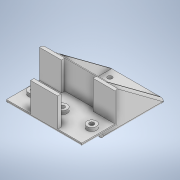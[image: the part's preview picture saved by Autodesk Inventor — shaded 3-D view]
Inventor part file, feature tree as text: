
AUTODESK INVENTOR PART (.ipt)
format: ipt  version: 2020 (Build 240168000, 168)  size: 404,992 bytes
history: native  units: in
note: dims shown in document units (in); Inventor stores cm internally (conversion verified against a paired STEP export)
features: sketch x19, extrude x18, fillet x1
ambient origin geometry x8: Origin, YZ Plane, XZ Plane, XY Plane, X Axis, Y Axis, Z Axis, Center Point
bodies: Solid1 (feature_tree)
feature tree (38):
  extrude  "Extrusion1"  Depth=1.2756in
  extrude  "Extrusion3"  Depth=0.1181in
  extrude  "Extrusion4"  Depth=1.0in TaperAngle=0.0deg
  extrude  "Extrusion5"  Depth=0.1181in TaperAngle=0.0deg
  extrude  "Extrusion6"  Depth=0.1181in TaperAngle=0.0deg
  extrude  "Extrusion9"  Depth=0.3346in
  extrude  "Extrusion10"  Depth=1.0236in
  extrude  "Extrusion11"  Depth=0.2953in
  extrude  "Extrusion14"  Depth=0.3346in
  extrude  "Extrusion15"  Depth=0.7677in
  extrude  "Extrusion16"  Depth=1.0in TaperAngle=0.0deg
  sketch  "Sketch17"  dims[d50=0.1772in d51=0.0in d54=0.1575in]
  extrude  "Extrusion17"  Depth=0.1575in
  extrude  "Extrusion18"  Depth=0.1575in
  extrude  "Extrusion20"  Depth=0.3937in
  extrude  "Extrusion21"  Depth=0.2362in
  extrude  "Extrusion22"  Depth=1.9291in
  extrude  "Extrusion23"  Depth=0.1969in
  extrude  "Extrusion24"  Depth=0.1969in
  fillet  "Fillet3"  Radius=0.4724in
  sketch  "Sketch1"  dims[d0=1.6142in d1=1.2756in]
  sketch  "Sketch3"  dims[d2=0.1181in d3=0.0in d8=0.1181in]
  sketch  "Sketch4"  dims[d9=0.1181in d10=1.0in d11=0.0in]
  sketch  "Sketch5"  dims[d12=0.8465in d13=0.1181in d14=0.0in]
  sketch  "Sketch6"  dims[d15=0.8465in d16=0.1181in d17=0.0in]
  sketch  "Sketch9"  dims[d20=0.3346in d21=0.3346in]
  sketch  "Sketch10"  dims[d22=0.1181in d23=0.0in d32=1.0236in]
  sketch  "Sketch11"  dims[d33=0.2953in d34=0.2953in]
  sketch  "Sketch14"  dims[d35=1.0236in d36=0.0in d37=0.3346in]
  sketch  "Sketch15"  dims[d38=0.1181in d39=0.0in d40=0.7677in]
  sketch  "Sketch16"  dims[d41=0.1181in d42=1.0in d43=0.0in]
  sketch  "Sketch18"  dims[d55=0.1575in d56=0.1575in]
  sketch  "Sketch19"  dims[d57=0.3937in d58=0.0in d59=0.2362in]
  sketch  "Sketch21"  dims[d60=0.2362in d61=0.2362in]
  sketch  "Sketch22"  dims[d62=0.1181in d63=0.0in d64=1.9291in]
  sketch  "Sketch23"  dims[d65=0.1969in d66=0.1969in]
  sketch  "Sketch24"  dims[d67=0.1969in d68=0.1969in d69=0.4724in d70=0.0in]
  sketch  "Sketch25"  dims[d71=0.1575in d72=0.1181in d73=0.1181in d74=1.9291in d75=0.0in d78=0.1181in d79=1.4331in d80=0.0in d81=1.9685in d82=0.0in d83=1.9685in d84=0.0in d85=0.315in d86=0.315in d87=0.315in d88=0.315in d89=0.2362in d90=0.2362in d91=0.2362in d92=0.2362in d93=0.1181in d94=0.0in d95=0.1575in d96=0.1575in d97=0.1575in d98=0.1575in d99=0.9843in d100=0.1969in d101=0.0in d102=0.0787in d44=0.0197in d45=0.0344in]
